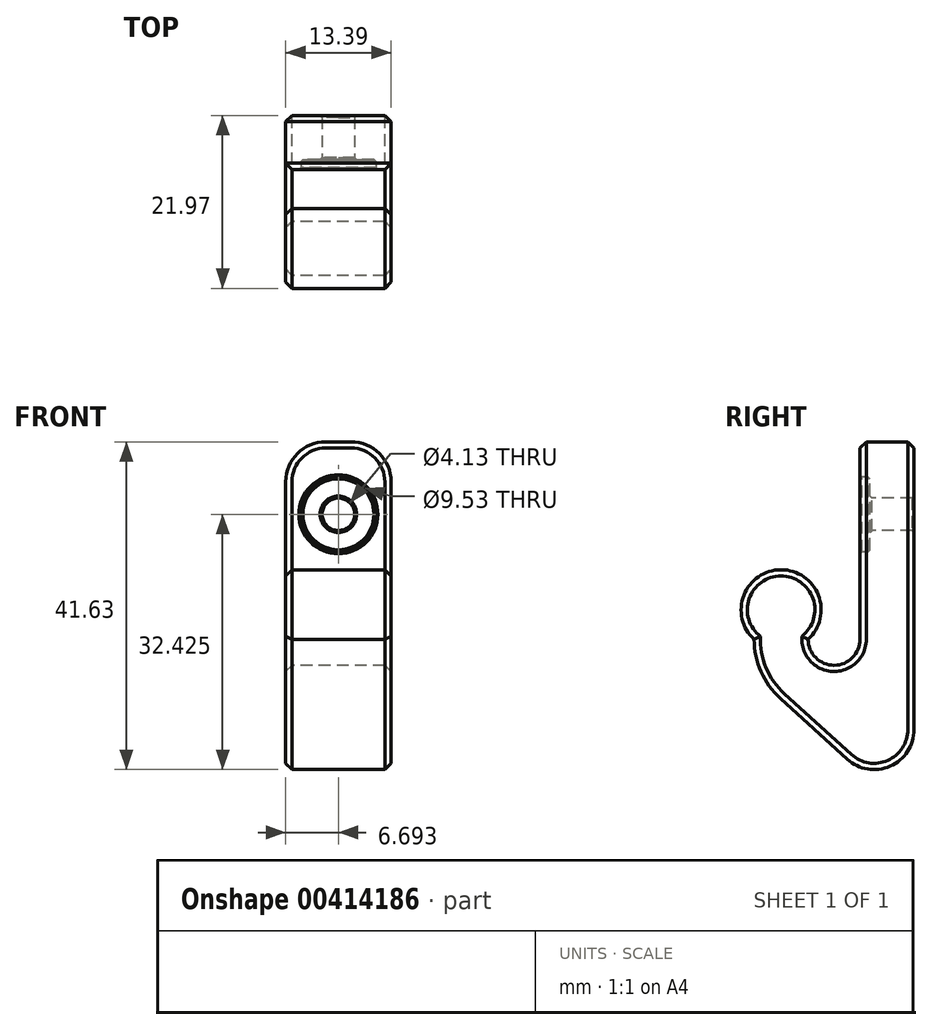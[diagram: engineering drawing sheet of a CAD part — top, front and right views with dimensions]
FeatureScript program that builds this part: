
annotation { "Feature Type Name" : "Feature", "Feature Type Description" : "" }
export const myFeature = defineFeature(function(context is Context, id is Id, definition is map)
    precondition{}
    {
        {
            var Q0;
            Q0=qCreatedBy(makeId("Right.planeOp"),FACE);
            var sketch = newSketch(context, id + "F0", { "sketchPlane" : qUnion([Q0])});
            skLineSegment(sketch, "E0", {"start": v(10.16, 25.08) * mm, "end": v(10.16, -22.95) * mm});
            skArc(sketch, "E1", {"start": v(-3.3, 0) * mm, "mid": v(0, -3.3) * mm, "end": v(3.3, 0) * mm});
            skArc(sketch, "E2", {"start": v(-10.16, 0) * mm, "mid": v(-9.3, -4.11) * mm, "end": v(-6.83, -7.52) * mm});
            skLineSegment(sketch, "E3", {"start": v(3.3, 25.08) * mm, "end": v(10.16, 25.08) * mm});
            skLineSegment(sketch, "E4", {"start": v(3.3, 0) * mm, "end": v(3.3, 25.08) * mm});
            skLineSegment(sketch, "E5", {"start": v(10.16, -22.95) * mm, "end": v(-6.83, -7.52) * mm});
            skArc(sketch, "E6", {"start": v(-3.3, 0) * mm, "mid": v(-6.73, 8.83) * mm, "end": v(-10.16, 0) * mm});
            skPoint(sketch, "E7.orphan", {"position": v(-3.3, 0) * mm});
            skLineSegment(sketch, "E8", {"start": v(-10.16, 0) * mm, "end": v(-3.3, 0) * mm, "construction": true});
            skLineSegment(sketch, "E9", {"start": v(-6.73, 0) * mm, "end": v(-6.73, 3.75) * mm, "construction": true});
            skSolve(sketch);
        }
        {
            var Q0;
            Q0 = qSketchRegion(id + "F0", true);
            extrude(context, id + "F1", {"entities" : qUnion([Q0]), "depth" : 13.4 * mm, "offsetDistance" : 25.4 * mm});
        }
        {
            var Q0;
            Q0=makeQuery(id+"F1.opExtrude","SWEPT_EDGE",EDGE,{"disambiguationData":[OSD([sQuery(id+"F0.wireOp",EDGE,"E0"),sQuery(id+"F0.wireOp",EDGE,"E5")])]});
            var Q1;
            Q1=makeQuery(id+"F1.opExtrude","CAP_EDGE",EDGE,{"disambiguationData":[OSD([sQuery(id+"F0.wireOp",EDGE,"E3")])],"isStart":false});
            var Q2;
            Q2=makeQuery(id+"F1.opExtrude","CAP_EDGE",EDGE,{"disambiguationData":[OSD([sQuery(id+"F0.wireOp",EDGE,"E3")])],"isStart":true});
            fillet(context, id + "F2", {"entities" : qUnion([Q0, Q1, Q2]), "tangentPropagation" : true, "radius" : 5.08 * mm, "defaultsChanged" : false, "vertexSettings" : [], "allowEdgeOverflow" : false});
        }
        {
            var Q0;
            Q0=makeQuery(id+"F1.opExtrude","SWEPT_FACE",FACE,{"disambiguationData":[OSD([sQuery(id+"F0.wireOp",EDGE,"E4")])]});
            var sketch = newSketch(context, id + "F3", { "sketchPlane" : qUnion([Q0])});
            skCircle(sketch, "E10", {"center": v(6.7, 15.88) * mm, "radius": 2.06 * mm});
            skPoint(sketch, "E10.centerSnap0", {"position": v(6.7, 0) * mm});
            skSolve(sketch);
        }
        {
            var Q0;
            Q0 = qSketchRegion(id + "F3", true);
            extrude(context, id + "F4", {"entities" : qUnion([Q0]), "operationType" : NewBodyOperationType.REMOVE, "oppositeDirection" : true, "depth" : 25.4 * mm, "offsetDistance" : 25.4 * mm});
        }
        {
            var Q0;
            Q0=makeQuery(id+"F1.opExtrude","SWEPT_FACE",FACE,{"disambiguationData":[OSD([sQuery(id+"F0.wireOp",EDGE,"E4")])]});
            var sketch = newSketch(context, id + "F5", { "sketchPlane" : qUnion([Q0])});
            skCircle(sketch, "E11", {"center": v(6.7, 15.88) * mm, "radius": 4.76 * mm});
            skSolve(sketch);
        }
        {
            var Q0;
            Q0 = qSketchRegion(id + "F5", true);
            extrude(context, id + "F6", {"entities" : qUnion([Q0]), "operationType" : NewBodyOperationType.REMOVE, "oppositeDirection" : true, "depth" : 1.27 * mm, "offsetDistance" : 25.4 * mm});
        }
        {
            var Q0;
            Q0=makeQuery(id+"F1.opExtrude","CAP_FACE",FACE,{"disambiguationData":[OSD([sQuery(id+"F0.wireOp",EDGE,"E0"),sQuery(id+"F0.wireOp",EDGE,"E1"),sQuery(id+"F0.wireOp",EDGE,"E2"),sQuery(id+"F0.wireOp",EDGE,"E3"),sQuery(id+"F0.wireOp",EDGE,"E4"),sQuery(id+"F0.wireOp",EDGE,"E5"),sQuery(id+"F0.wireOp",EDGE,"E6")])],"isStart":false});
            var Q1;
            Q1=makeQuery(id+"F1.opExtrude","CAP_FACE",FACE,{"disambiguationData":[OSD([sQuery(id+"F0.wireOp",EDGE,"E0"),sQuery(id+"F0.wireOp",EDGE,"E1"),sQuery(id+"F0.wireOp",EDGE,"E2"),sQuery(id+"F0.wireOp",EDGE,"E3"),sQuery(id+"F0.wireOp",EDGE,"E4"),sQuery(id+"F0.wireOp",EDGE,"E5"),sQuery(id+"F0.wireOp",EDGE,"E6")])],"isStart":true});
            chamfer(context, id + "F7", {"entities" : qUnion([Q0, Q1]), "width" : 0.8 * mm, "tangentPropagation" : true});
        }
        {
            var Q0;
            Q0=makeQuery(id+"F6.boolean.opBoolean","COPY",FACE,{"derivedFrom":makeQuery(id+"F6.opExtrude","SWEPT_FACE",FACE,{"disambiguationData":[OSD([sQuery(id+"F5.wireOp",EDGE,"E11")])]})});
            var Q1;
            Q1=makeQuery(id+"F4.boolean.opBoolean","COPY",FACE,{"derivedFrom":makeQuery(id+"F4.opExtrude","SWEPT_FACE",FACE,{"disambiguationData":[OSD([sQuery(id+"F3.wireOp",EDGE,"E10")])]})});
            chamfer(context, id + "F8", {"entities" : qUnion([Q0, Q1]), "width" : 0.25 * mm, "tangentPropagation" : true});
        }
    });
